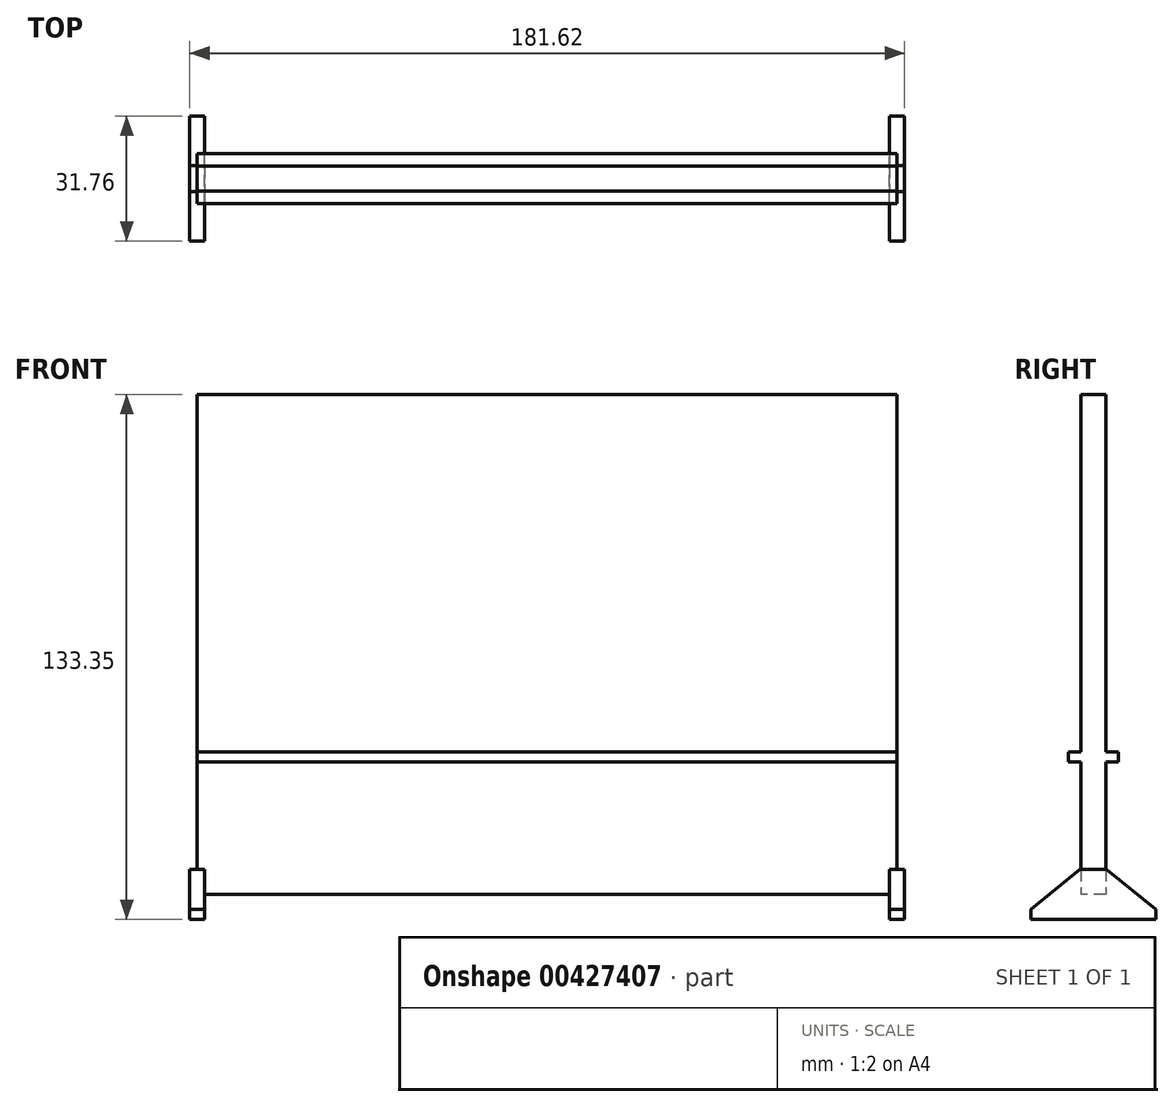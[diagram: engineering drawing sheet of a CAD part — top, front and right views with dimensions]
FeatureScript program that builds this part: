
annotation { "Feature Type Name" : "Feature", "Feature Type Description" : "" }
export const myFeature = defineFeature(function(context is Context, id is Id, definition is map)
    precondition{}
    {
        {
            var Q0;
            Q0=qCreatedBy(makeId("Right.planeOp"),FACE);
            var sketch = newSketch(context, id + "F0", { "sketchPlane" : qUnion([Q0])});
            skLineSegment(sketch, "E0.bottom", {"start": v(-3.17, -63.5) * mm, "end": v(3.18, -63.5) * mm});
            skLineSegment(sketch, "E0.top", {"start": v(-3.18, 63.5) * mm, "end": v(3.17, 63.5) * mm});
            skLineSegment(sketch, "E0.left", {"start": v(-3.17, -63.5) * mm, "end": v(-3.18, 63.5) * mm});
            skLineSegment(sketch, "E0.right", {"start": v(3.18, -63.5) * mm, "end": v(3.17, 63.5) * mm});
            skPoint(sketch, "E0.middle", {"position": v(0, 0) * mm});
            skSolve(sketch);
        }
        {
            var Q0;
            Q0 = qSketchRegion(id + "F0", true);
            extrude(context, id + "F1", {"entities" : qUnion([Q0]), "depth" : 177.8 * mm});
        }
        {
            var Q0;
            Q0=makeQuery(id+"F1.opExtrude","SWEPT_FACE",FACE,{"disambiguationData":[OSD([sQuery(id+"F0.wireOp",EDGE,"E0.left")])]});
            var sketch = newSketch(context, id + "F2", { "sketchPlane" : qUnion([Q0])});
            skLineSegment(sketch, "E1.bottom", {"start": v(1.9, -69.85) * mm, "end": v(-1.9, -69.85) * mm});
            skLineSegment(sketch, "E1.top", {"start": v(1.9, -57.15) * mm, "end": v(-1.9, -57.15) * mm});
            skLineSegment(sketch, "E1.left", {"start": v(1.9, -69.85) * mm, "end": v(1.9, -57.15) * mm});
            skLineSegment(sketch, "E1.right", {"start": v(-1.9, -69.85) * mm, "end": v(-1.9, -57.15) * mm});
            skPoint(sketch, "E1.middle", {"position": v(0, -63.5) * mm});
            skLineSegment(sketch, "E2.bottom", {"start": v(179.7, -69.85) * mm, "end": v(175.9, -69.85) * mm});
            skLineSegment(sketch, "E2.top", {"start": v(179.7, -57.15) * mm, "end": v(175.9, -57.15) * mm});
            skLineSegment(sketch, "E2.left", {"start": v(179.7, -69.85) * mm, "end": v(179.7, -57.15) * mm});
            skLineSegment(sketch, "E2.right", {"start": v(175.9, -69.85) * mm, "end": v(175.9, -57.15) * mm});
            skPoint(sketch, "E2.middle", {"position": v(177.8, -63.5) * mm});
            skSolve(sketch);
        }
        {
            var Q0;
            Q0 = qSketchRegion(id + "F2", true);
            extrude(context, id + "F3", {"entities" : qUnion([Q0]), "operationType" : NewBodyOperationType.ADD, "depth" : 12.7 * mm, "hasSecondDirection" : true, "secondDirectionOppositeDirection" : true, "secondDirectionDepth" : 19.05 * mm});
        }
        {
            var Q0;
            Q0=makeQuery(id+"F3.opExtrude","CAP_EDGE",EDGE,{"disambiguationData":[OSD([sQuery(id+"F2.wireOp",EDGE,"E2.top")])],"isStart":false});
            var Q1;
            Q1=makeQuery(id+"F3.opExtrude","CAP_EDGE",EDGE,{"disambiguationData":[OSD([sQuery(id+"F2.wireOp",EDGE,"E2.top")])],"isStart":true});
            var Q2;
            Q2=makeQuery(id+"F3.opExtrude","CAP_EDGE",EDGE,{"disambiguationData":[OSD([sQuery(id+"F2.wireOp",EDGE,"E1.top")])],"isStart":false});
            chamfer(context, id + "F4", {"entities" : qUnion([Q0, Q1, Q2]), "chamferType" : ChamferType.OFFSET_ANGLE, "width" : 10.16 * mm, "oppositeDirection" : false, "angle" : 51 * degree, "tangentPropagation" : true});
        }
        {
            var Q0;
            Q0=makeQuery(id+"F3.opExtrude","CAP_EDGE",EDGE,{"disambiguationData":[OSD([sQuery(id+"F2.wireOp",EDGE,"E1.top")])],"isStart":true});
            chamfer(context, id + "F5", {"entities" : qUnion([Q0]), "chamferType" : ChamferType.OFFSET_ANGLE, "width" : 10.16 * mm, "oppositeDirection" : true, "angle" : 51 * degree, "tangentPropagation" : true});
        }
        {
            var Q0;
            Q0=makeQuery(id+"F1.opExtrude","CAP_FACE",FACE,{"disambiguationData":[OSD([sQuery(id+"F0.wireOp",EDGE,"E0.bottom"),sQuery(id+"F0.wireOp",EDGE,"E0.top"),sQuery(id+"F0.wireOp",EDGE,"E0.left"),sQuery(id+"F0.wireOp",EDGE,"E0.right")])],"isStart":false});
            var sketch = newSketch(context, id + "F6", { "sketchPlane" : qUnion([Q0])});
            skLineSegment(sketch, "E3", {"start": v(0, 0) * mm, "end": v(0, -57.15) * mm});
            skLineSegment(sketch, "E4", {"start": v(0, -57.15) * mm, "end": v(0, -28.58) * mm});
            skPoint(sketch, "E5.middle", {"position": v(0, -28.58) * mm});
            skLineSegment(sketch, "E6.bottom", {"start": v(6.35, -29.85) * mm, "end": v(-6.35, -29.85) * mm});
            skLineSegment(sketch, "E6.top", {"start": v(6.35, -27.3) * mm, "end": v(-6.35, -27.3) * mm});
            skLineSegment(sketch, "E6.left", {"start": v(6.35, -29.85) * mm, "end": v(6.35, -27.3) * mm});
            skLineSegment(sketch, "E6.right", {"start": v(-6.35, -29.85) * mm, "end": v(-6.35, -27.3) * mm});
            skSolve(sketch);
        }
        {
            var Q0;
            Q0 = qSketchRegion(id + "F6", true);
            extrude(context, id + "F7", {"entities" : qUnion([Q0]), "operationType" : NewBodyOperationType.ADD, "depth" : -177.8 * mm});
        }
    });
